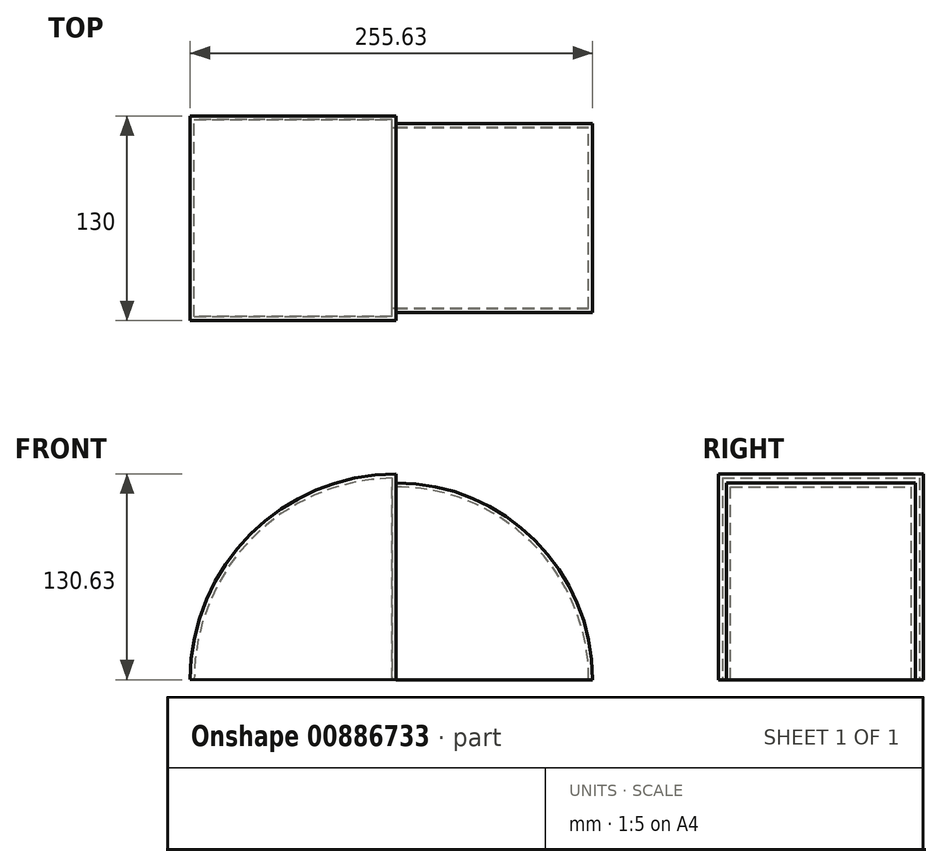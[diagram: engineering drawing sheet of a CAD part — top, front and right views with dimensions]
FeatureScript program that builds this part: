
annotation { "Feature Type Name" : "Feature", "Feature Type Description" : "" }
export const myFeature = defineFeature(function(context is Context, id is Id, definition is map)
    precondition{}
    {
        {
            var Q0;
            Q0=qCreatedBy(makeId("Front.planeOp"),FACE);
            var sketch = newSketch(context, id + "F0", { "sketchPlane" : qUnion([Q0])});
            skArc(sketch, "E0", {"start": v(125, 0) * mm, "mid": v(88.39, 88.39) * mm, "end": v(0, 125) * mm});
            skLineSegment(sketch, "E1", {"start": v(0, 0) * mm, "end": v(-125, 0) * mm});
            skLineSegment(sketch, "E2", {"start": v(-125, 0) * mm, "end": v(125, 0) * mm});
            skArc(sketch, "E3", {"start": v(0, 128.03) * mm, "mid": v(-90.47, 90.6) * mm, "end": v(-128.03, 0.18) * mm});
            skLineSegment(sketch, "E4", {"start": v(0, 0) * mm, "end": v(0, 125) * mm});
            skPoint(sketch, "E4.endSnap0", {"position": v(0, 125) * mm});
            skArc(sketch, "E5", {"start": v(0, 130.63) * mm, "mid": v(-92.3, 92.43) * mm, "end": v(-130.63, 0.18) * mm});
            skPoint(sketch, "E6", {"position": v(0, 62.5) * mm});
            skLineSegment(sketch, "E7", {"start": v(0, 0) * mm, "end": v(-90.47, 90.6) * mm});
            skLineSegment(sketch, "E8", {"start": v(-128.03, 0.18) * mm, "end": v(-130.63, 0.18) * mm});
            skLineSegment(sketch, "E9", {"start": v(-130.63, 0.18) * mm, "end": v(0, 0) * mm});
            skLineSegment(sketch, "E10", {"start": v(0, 130.63) * mm, "end": v(0, 128.03) * mm});
            skLineSegment(sketch, "E11.trimOffspring", {"start": v(0, 125) * mm, "end": v(0, 0) * mm});
            skLineSegment(sketch, "E12", {"start": v(0, 128.03) * mm, "end": v(0, 0) * mm});
            skSolve(sketch);
        }
        {
            var Q0;
            Q0=makeQuery(id+"F0.imprint","IMPRINT",FACE,{"disambiguationData":[TD([[makeQuery(id+"F0.imprint","IMPRINT",EDGE,{"derivedFrom":sQuery(id+"F0.wireOp",EDGE,"E0")}),1.0]])]});
            extrude(context, id + "F1", {"entities" : qUnion([Q0]), "endBound" : BoundingType.SYMMETRIC, "depth" : 120 * mm, "offsetDistance" : 25 * mm});
        }
        {
            var Q0;
            Q0=makeQuery(id+"F0.imprint","IMPRINT",FACE,{"disambiguationData":[TD([[makeQuery(id+"F0.imprint","IMPRINT",EDGE,{"derivedFrom":sQuery(id+"F0.wireOp",EDGE,"E4")}),1.0]])]});
            var Q1;
            {var subQ2=sQuery(id+"F0.wireOp",EDGE,"E7");Q1=makeQuery(id+"F0.imprint","IMPRINT",FACE,{"disambiguationData":[TD([[makeQuery(id+"F0.imprint","IMPRINT",EDGE,{"derivedFrom":subQ2}),1.0]])]});}
            var Q2;
            Q2=makeQuery(id+"F0.imprint","IMPRINT",FACE,{"disambiguationData":[TD([[makeQuery(id+"F0.imprint","IMPRINT",EDGE,{"derivedFrom":sQuery(id+"F0.wireOp",EDGE,"E5")}),1.0]])]});
            extrude(context, id + "F2", {"entities" : qUnion([Q0, Q1, Q2]), "operationType" : NewBodyOperationType.ADD, "endBound" : BoundingType.SYMMETRIC, "depth" : 130 * mm, "offsetDistance" : 25 * mm});
        }
        {
            var Q0;
            Q0=makeQuery(id+"F2.opExtrude","SWEPT_FACE",FACE,{"disambiguationData":[OSD([sQuery(id+"F0.wireOp",EDGE,"E9")])]});
            var Q1;
            Q1=makeQuery(id+"F1.opExtrude","SWEPT_FACE",FACE,{"disambiguationData":[OSD([sQuery(id+"F0.wireOp",EDGE,"E2")])]});
            shell(context, id + "F3", {"entities" : qUnion([Q0, Q1]), "thickness" : 2.5 * mm});
        }
    });
